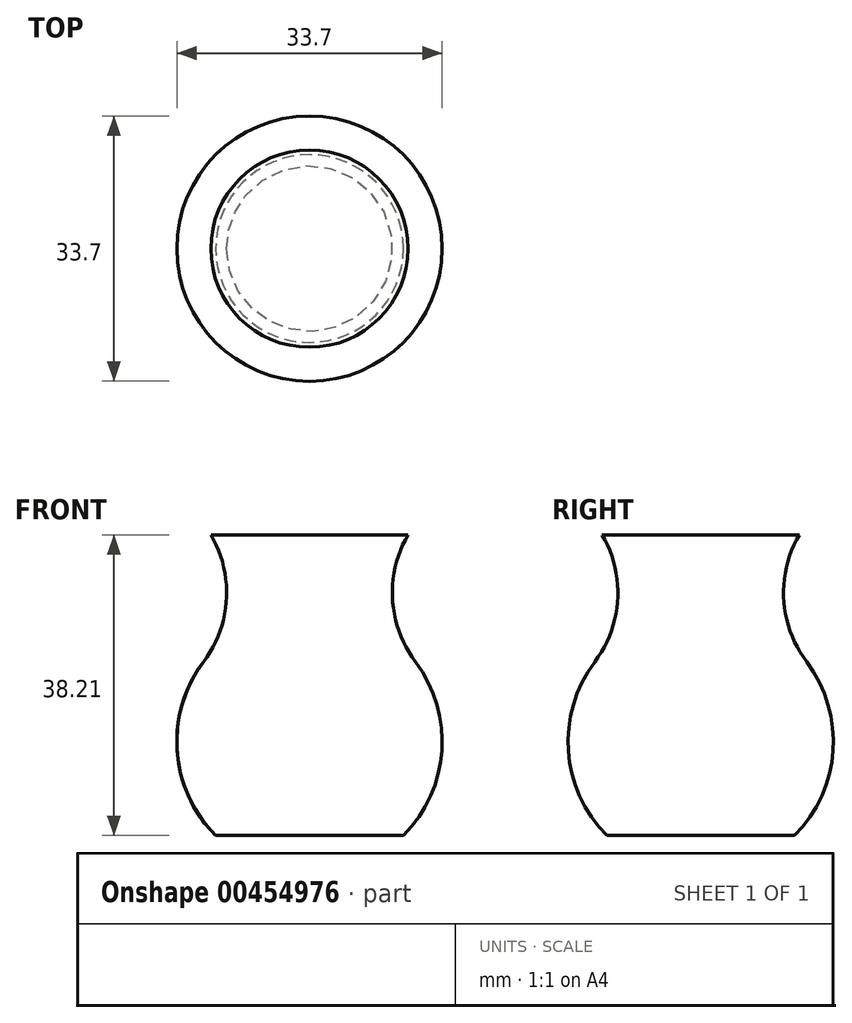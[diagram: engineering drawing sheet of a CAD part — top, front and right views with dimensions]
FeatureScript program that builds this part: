
annotation { "Feature Type Name" : "Feature", "Feature Type Description" : "" }
export const myFeature = defineFeature(function(context is Context, id is Id, definition is map)
    precondition{}
    {
        {
            var Q0;
            Q0=qCreatedBy(makeId("Front.planeOp"),FACE);
            var sketch = newSketch(context, id + "F0", { "sketchPlane" : qUnion([Q0])});
            skLineSegment(sketch, "E0", {"start": v(0, 0) * mm, "end": v(0, 38.21) * mm});
            skLineSegment(sketch, "E1", {"start": v(0, 0) * mm, "end": v(-11.92, 0) * mm});
            skLineSegment(sketch, "E2", {"start": v(-11.92, 0) * mm, "end": v(-6.76, -5.15) * mm, "construction": true});
            skArc(sketch, "E3", {"start": v(-11.92, 0) * mm, "mid": v(-16.81, 10.74) * mm, "end": v(-13.46, 22.06) * mm});
            skArc(sketch, "E4", {"start": v(-13.46, 22.06) * mm, "mid": v(-10.55, 30) * mm, "end": v(-12.53, 38.21) * mm});
            skLineSegment(sketch, "E5", {"start": v(-12.53, 38.21) * mm, "end": v(0, 38.21) * mm});
            skSolve(sketch);
        }
        {
            var Q0;
            Q0=makeQuery(id+"F0.imprint","IMPRINT",FACE,{"disambiguationData":[TD([[makeQuery(id+"F0.imprint","IMPRINT",EDGE,{"derivedFrom":sQuery(id+"F0.wireOp",EDGE,"E0")}),1.0]])]});
            var Q1;
            Q1=sQuery(id+"F0.wireOp",EDGE,"E0");
            revolve(context, id + "F1", {"entities" : qUnion([Q0]), "axis" : qUnion([Q1]), "revolveType" : RevolveType.FULL});
        }
    });
